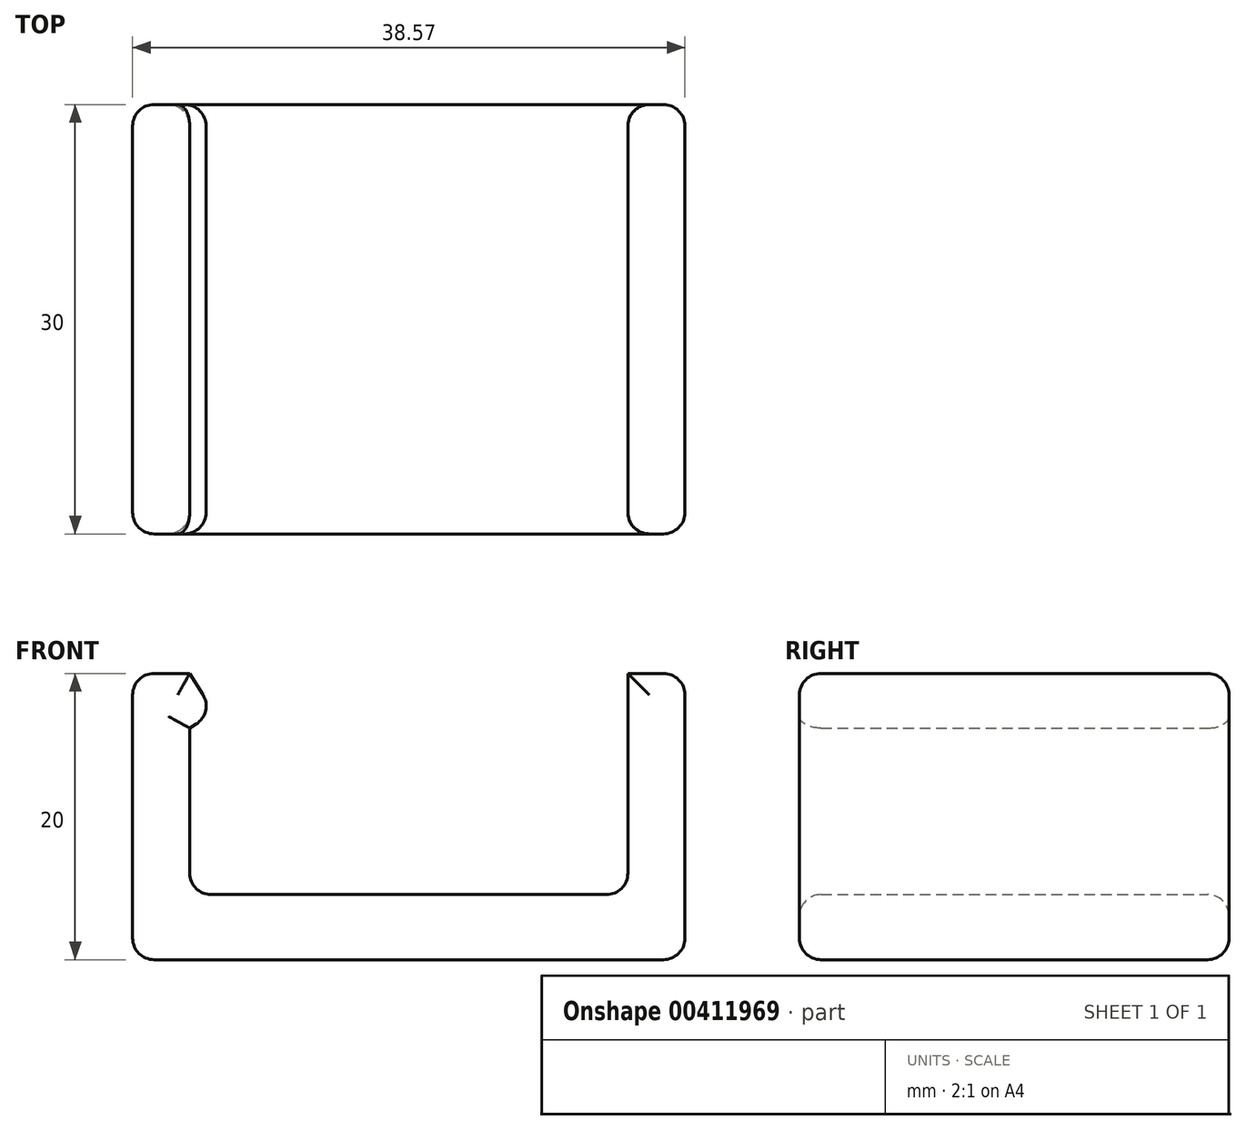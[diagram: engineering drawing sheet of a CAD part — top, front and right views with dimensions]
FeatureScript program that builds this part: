
annotation { "Feature Type Name" : "Feature", "Feature Type Description" : "" }
export const myFeature = defineFeature(function(context is Context, id is Id, definition is map)
    precondition{}
    {
        {
            var Q0;
            Q0=qCreatedBy(makeId("Front.planeOp"),FACE);
            var sketch = newSketch(context, id + "F0", { "sketchPlane" : qUnion([Q0])});
            skLineSegment(sketch, "E0", {"start": v(-52.13, 53.73) * mm, "end": v(-52.13, 36.73) * mm});
            skLineSegment(sketch, "E1", {"start": v(-48.14, 51.4) * mm, "end": v(-48.14, 41.28) * mm});
            skLineSegment(sketch, "E2", {"start": v(-50.63, 55.23) * mm, "end": v(-48.14, 55.23) * mm});
            skLineSegment(sketch, "E3", {"start": v(-48.14, 55.23) * mm, "end": v(-47.22, 53.75) * mm});
            skLineSegment(sketch, "E4", {"start": v(-47.7, 51.68) * mm, "end": v(-48.14, 51.4) * mm});
            skPoint(sketch, "E5.visualSharp", {"position": v(-46.43, 52.48) * mm});
            skArc(sketch, "E5.filletArc", {"start": v(-47.7, 51.68) * mm, "mid": v(-47.03, 52.62) * mm, "end": v(-47.22, 53.75) * mm});
            skPoint(sketch, "E6.visualSharp", {"position": v(-52.13, 55.23) * mm});
            skArc(sketch, "E6.filletArc", {"start": v(-50.63, 55.23) * mm, "mid": v(-51.69, 54.8) * mm, "end": v(-52.13, 53.73) * mm});
            skArc(sketch, "E7.filletArc", {"start": v(-52.13, 36.73) * mm, "mid": v(-51.69, 35.67) * mm, "end": v(-50.63, 35.23) * mm});
            skArc(sketch, "E8.filletArc", {"start": v(-48.14, 41.28) * mm, "mid": v(-47.7, 40.22) * mm, "end": v(-46.64, 39.78) * mm});
            skArc(sketch, "E9.MirrorCS", {"start": v(-13.56, 36.73) * mm, "mid": v(-14, 35.67) * mm, "end": v(-15.06, 35.23) * mm});
            skLineSegment(sketch, "E10.MirrorCS", {"start": v(-13.56, 53.73) * mm, "end": v(-13.56, 36.73) * mm});
            skArc(sketch, "E11.MirrorCS", {"start": v(-15.06, 55.23) * mm, "mid": v(-14, 54.8) * mm, "end": v(-13.56, 53.73) * mm});
            skArc(sketch, "E12.MirrorCS", {"start": v(-17.54, 41.28) * mm, "mid": v(-17.98, 40.22) * mm, "end": v(-19.04, 39.78) * mm});
            skPoint(sketch, "E13.MirrorP", {"position": v(-13.56, 35.23) * mm});
            skLineSegment(sketch, "E14.MirrorCS", {"start": v(-15.06, 55.23) * mm, "end": v(-17.54, 55.23) * mm});
            skPoint(sketch, "E15.MirrorP", {"position": v(-13.56, 55.23) * mm});
            skPoint(sketch, "E16.MirrorCS.end.orphan", {"position": v(-18.46, 53.75) * mm});
            skPoint(sketch, "E16.MirrorCS.start.orphan", {"position": v(-17.54, 55.23) * mm});
            skPoint(sketch, "E17.MirrorCS.end.orphan", {"position": v(-17.54, 41.28) * mm});
            skPoint(sketch, "E18.end.orphan", {"position": v(-17.54, 51.4) * mm});
            skPoint(sketch, "E18.start.orphan", {"position": v(-17.99, 51.68) * mm});
            skLineSegment(sketch, "E19", {"start": v(-17.54, 55.23) * mm, "end": v(-17.54, 41.28) * mm});
            skPoint(sketch, "E20.MirrorCS.start.orphan", {"position": v(-19.04, 39.78) * mm});
            skLineSegment(sketch, "E21", {"start": v(-46.64, 39.78) * mm, "end": v(-19.04, 39.78) * mm});
            skLineSegment(sketch, "E22", {"start": v(-50.63, 35.23) * mm, "end": v(-15.06, 35.23) * mm});
            skSolve(sketch);
        }
        {
            var Q0;
            Q0=makeQuery(id+"F0.imprint","IMPRINT",FACE,{"disambiguationData":[TD([[makeQuery(id+"F0.imprint","IMPRINT",EDGE,{"derivedFrom":sQuery(id+"F0.wireOp",EDGE,"E0")}),1.0]])]});
            extrude(context, id + "F1", {"entities" : qUnion([Q0]), "depth" : 30 * mm});
        }
        {
            var Q0;
            Q0=makeQuery(id+"F1.opExtrude","SWEPT_FACE",FACE,{"disambiguationData":[OSD([sQuery(id+"F0.wireOp",EDGE,"1g7yY4Lf-N2nS-Ciid-9dXl-rYSCJ1U4e6md"),sQuery(id+"F0.wireOp",EDGE,"E20.MirrorCS")])]});
            var Q1;
            Q1=makeQuery(id+"F1.opExtrude","CAP_FACE",FACE,{"disambiguationData":[OSD([sQuery(id+"F0.wireOp",EDGE,"E0"),sQuery(id+"F0.wireOp",EDGE,"hD5B07b9-8fB3-ab8F-OQBz-6AUuHvz6sJ98"),sQuery(id+"F0.wireOp",EDGE,"E1"),sQuery(id+"F0.wireOp",EDGE,"1g7yY4Lf-N2nS-Ciid-9dXl-rYSCJ1U4e6md"),sQuery(id+"F0.wireOp",EDGE,"E2"),sQuery(id+"F0.wireOp",EDGE,"E3"),sQuery(id+"F0.wireOp",EDGE,"E4"),sQuery(id+"F0.wireOp",EDGE,"E5.filletArc"),sQuery(id+"F0.wireOp",EDGE,"E6.filletArc"),sQuery(id+"F0.wireOp",EDGE,"E7.filletArc"),sQuery(id+"F0.wireOp",EDGE,"E8.filletArc"),sQuery(id+"F0.wireOp",EDGE,"E20.MirrorCS"),sQuery(id+"F0.wireOp",EDGE,"E9.MirrorCS"),sQuery(id+"F0.wireOp",EDGE,"a740919c-cbcc-4286-9e3f-5fc87413fc890.MirrorCS"),sQuery(id+"F0.wireOp",EDGE,"E10.MirrorCS"),sQuery(id+"F0.wireOp",EDGE,"E11.MirrorCS"),sQuery(id+"F0.wireOp",EDGE,"E16.MirrorCS"),sQuery(id+"F0.wireOp",EDGE,"8ea7e99a-36cf-41ac-82d1-a3d94d0b58f00.MirrorCS"),sQuery(id+"F0.wireOp",EDGE,"E17.MirrorCS"),sQuery(id+"F0.wireOp",EDGE,"E12.MirrorCS"),sQuery(id+"F0.wireOp",EDGE,"E14.MirrorCS"),sQuery(id+"F0.wireOp",EDGE,"E18")])],"isStart":false});
            var Q2;
            Q2=makeQuery(id+"F1.opExtrude","CAP_FACE",FACE,{"disambiguationData":[OSD([sQuery(id+"F0.wireOp",EDGE,"E0"),sQuery(id+"F0.wireOp",EDGE,"hD5B07b9-8fB3-ab8F-OQBz-6AUuHvz6sJ98"),sQuery(id+"F0.wireOp",EDGE,"E1"),sQuery(id+"F0.wireOp",EDGE,"1g7yY4Lf-N2nS-Ciid-9dXl-rYSCJ1U4e6md"),sQuery(id+"F0.wireOp",EDGE,"E2"),sQuery(id+"F0.wireOp",EDGE,"E3"),sQuery(id+"F0.wireOp",EDGE,"E4"),sQuery(id+"F0.wireOp",EDGE,"E5.filletArc"),sQuery(id+"F0.wireOp",EDGE,"E6.filletArc"),sQuery(id+"F0.wireOp",EDGE,"E7.filletArc"),sQuery(id+"F0.wireOp",EDGE,"E8.filletArc"),sQuery(id+"F0.wireOp",EDGE,"E20.MirrorCS"),sQuery(id+"F0.wireOp",EDGE,"E9.MirrorCS"),sQuery(id+"F0.wireOp",EDGE,"a740919c-cbcc-4286-9e3f-5fc87413fc890.MirrorCS"),sQuery(id+"F0.wireOp",EDGE,"E10.MirrorCS"),sQuery(id+"F0.wireOp",EDGE,"E11.MirrorCS"),sQuery(id+"F0.wireOp",EDGE,"E16.MirrorCS"),sQuery(id+"F0.wireOp",EDGE,"8ea7e99a-36cf-41ac-82d1-a3d94d0b58f00.MirrorCS"),sQuery(id+"F0.wireOp",EDGE,"E17.MirrorCS"),sQuery(id+"F0.wireOp",EDGE,"E12.MirrorCS"),sQuery(id+"F0.wireOp",EDGE,"E14.MirrorCS"),sQuery(id+"F0.wireOp",EDGE,"E18")])],"isStart":true});
            fillet(context, id + "F2", {"entities" : qUnion([Q0, Q1, Q2]), "radius" : 1.5 * mm, "tangentPropagation" : true, "allowEdgeOverflow" : false});
        }
    });
